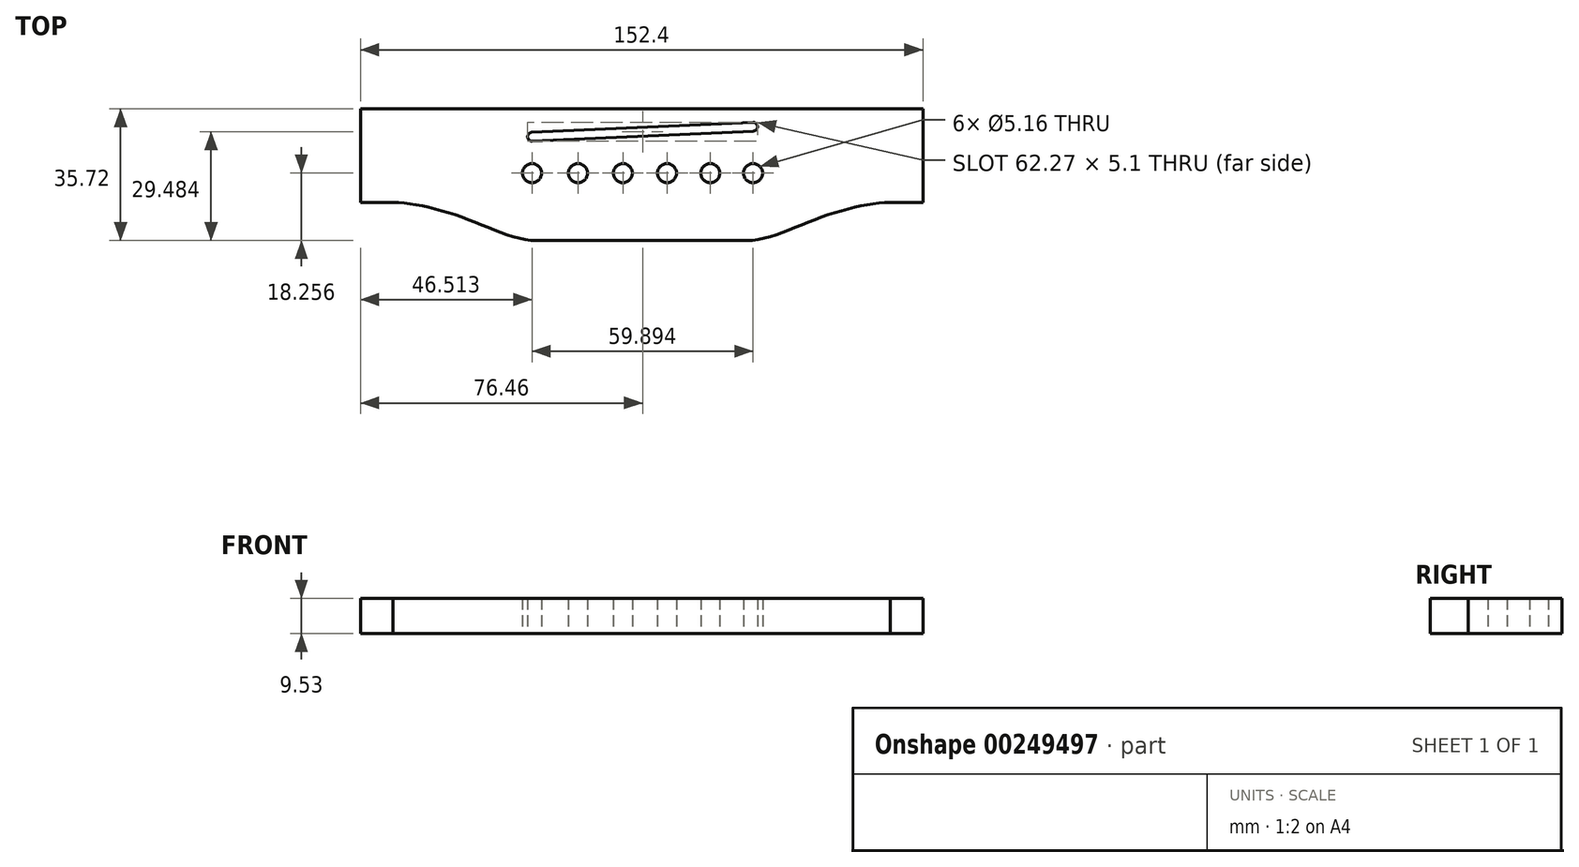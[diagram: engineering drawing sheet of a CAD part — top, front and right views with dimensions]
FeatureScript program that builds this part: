
annotation { "Feature Type Name" : "Feature", "Feature Type Description" : "" }
export const myFeature = defineFeature(function(context is Context, id is Id, definition is map)
    precondition{}
    {
        {
            var Q0;
            Q0=qCreatedBy(makeId("Top.planeOp"),FACE);
            var sketch = newSketch(context, id + "F0", { "sketchPlane" : qUnion([Q0])});
            skLineSegment(sketch, "E0", {"start": v(0, 41.58) * mm, "end": v(0, -43.57) * mm, "construction": true});
            skLineSegment(sketch, "E1", {"start": v(0, 35.72) * mm, "end": v(-76.2, 35.72) * mm});
            skLineSegment(sketch, "E2", {"start": v(-76.2, 35.72) * mm, "end": v(-76.2, 10.32) * mm});
            skLineSegment(sketch, "E3", {"start": v(0, 0) * mm, "end": v(-28.58, 0) * mm});
            skCircle(sketch, "E4", {"center": v(-29.69, 18.26) * mm, "radius": 2.58 * mm});
            skCircle(sketch, "E5.MirrorC", {"center": v(30.2, 18.26) * mm, "radius": 2.58 * mm});
            skLineSegment(sketch, "E6.MirrorCS", {"start": v(0, 35.72) * mm, "end": v(76.2, 35.72) * mm});
            skLineSegment(sketch, "E7.MirrorCS", {"start": v(76.2, 35.72) * mm, "end": v(76.2, 7.14) * mm});
            skLineSegment(sketch, "E8.MirrorCS", {"start": v(0, 0) * mm, "end": v(28.58, 0) * mm});
            skCircle(sketch, "E9", {"center": v(-17.25, 18.26) * mm, "radius": 2.58 * mm});
            skCircle(sketch, "E10", {"center": v(6.87, 18.26) * mm, "radius": 2.58 * mm});
            skCircle(sketch, "E11", {"center": v(18.62, 18.26) * mm, "radius": 2.58 * mm});
            skLineSegment(sketch, "E12", {"start": v(-66.56, 18.26) * mm, "end": v(70.4, 18.26) * mm, "construction": true});
            skCircle(sketch, "E13", {"center": v(-5.07, 18.26) * mm, "radius": 2.58 * mm});
            skCircle(sketch, "E14", {"center": v(-29.69, 18.26) * mm, "radius": 0.67 * mm});
            skCircle(sketch, "E15", {"center": v(-17.25, 18.26) * mm, "radius": 0.53 * mm});
            skCircle(sketch, "E16", {"center": v(-5.07, 18.26) * mm, "radius": 0.4 * mm});
            skCircle(sketch, "E17", {"center": v(6.87, 18.26) * mm, "radius": 0.3 * mm});
            skCircle(sketch, "E18", {"center": v(18.62, 18.26) * mm, "radius": 0.2 * mm});
            skCircle(sketch, "E19", {"center": v(30.2, 18.26) * mm, "radius": 0.15 * mm});
            skLineSegment(sketch, "E20", {"start": v(-76.2, 10.32) * mm, "end": v(-76.2, 7.14) * mm});
            skLineSegment(sketch, "E21", {"start": v(-76.2, 10.32) * mm, "end": v(-67.32, 10.32) * mm});
            skFitSpline(sketch, "E22", {"points": [v(-67.32, 10.32) * mm, v(-47.85, 6.02) * mm, v(-28.58, 0) * mm], "startDerivative": vector(32.7, -0.39) * mm, "endDerivative": vector(34, 0) * mm});
            skFitSpline(sketch, "E23.MirrorCS", {"points": [v(67.32, 10.32) * mm, v(47.85, 6.02) * mm, v(28.58, 0) * mm], "startDerivative": vector(-32.7, -0.39) * mm, "endDerivative": vector(-34, 0) * mm});
            skLineSegment(sketch, "E24.MirrorCS", {"start": v(76.2, 10.32) * mm, "end": v(67.32, 10.32) * mm});
            skLineSegment(sketch, "E25", {"start": v(-29.69, 18.26) * mm, "end": v(-29.69, 35.72) * mm, "construction": true});
            skLineSegment(sketch, "E26", {"start": v(-17.25, 18.26) * mm, "end": v(-17.25, 35.72) * mm, "construction": true});
            skLineSegment(sketch, "E27", {"start": v(-5.07, 18.26) * mm, "end": v(-5.07, 35.72) * mm, "construction": true});
            skLineSegment(sketch, "E28", {"start": v(6.87, 18.26) * mm, "end": v(6.87, 35.72) * mm, "construction": true});
            skLineSegment(sketch, "E29", {"start": v(18.62, 18.26) * mm, "end": v(18.62, 35.72) * mm, "construction": true});
            skLineSegment(sketch, "E30", {"start": v(30.2, 18.26) * mm, "end": v(30.2, 35.72) * mm, "construction": true});
            skPoint(sketch, "E31", {"position": v(-29.69, 26.93) * mm});
            skPoint(sketch, "E32", {"position": v(-17.25, 28.86) * mm});
            skPoint(sketch, "E33", {"position": v(-5.07, 29.98) * mm});
            skPoint(sketch, "E34", {"position": v(6.87, 30.84) * mm});
            skPoint(sketch, "E35", {"position": v(18.62, 29.04) * mm});
            skPoint(sketch, "E36", {"position": v(30.2, 31) * mm});
            skArc(sketch, "E37", {"start": v(-29.69, 29.31) * mm, "mid": v(-30.88, 28.1) * mm, "end": v(-29.63, 26.93) * mm});
            skArc(sketch, "E38", {"start": v(30.2, 29.66) * mm, "mid": v(31.4, 30.87) * mm, "end": v(30.15, 32.04) * mm});
            skLineSegment(sketch, "E39", {"start": v(-29.74, 29.31) * mm, "end": v(30.15, 32.04) * mm});
            skLineSegment(sketch, "E40", {"start": v(-29.63, 26.93) * mm, "end": v(30.26, 29.66) * mm});
            skPoint(sketch, "E41", {"position": v(0, 30.66) * mm});
            skSolve(sketch);
        }
        {
            var Q0;
            Q0=makeQuery(id+"F0.imprint","IMPRINT",FACE,{"disambiguationData":[TD([[makeQuery(id+"F0.imprint","IMPRINT",EDGE,{"derivedFrom":sQuery(id+"F0.wireOp",EDGE,"E1")}),1.0]])]});
            extrude(context, id + "F1", {"entities" : qUnion([Q0]), "depth" : 9.52 * mm});
        }
    });
